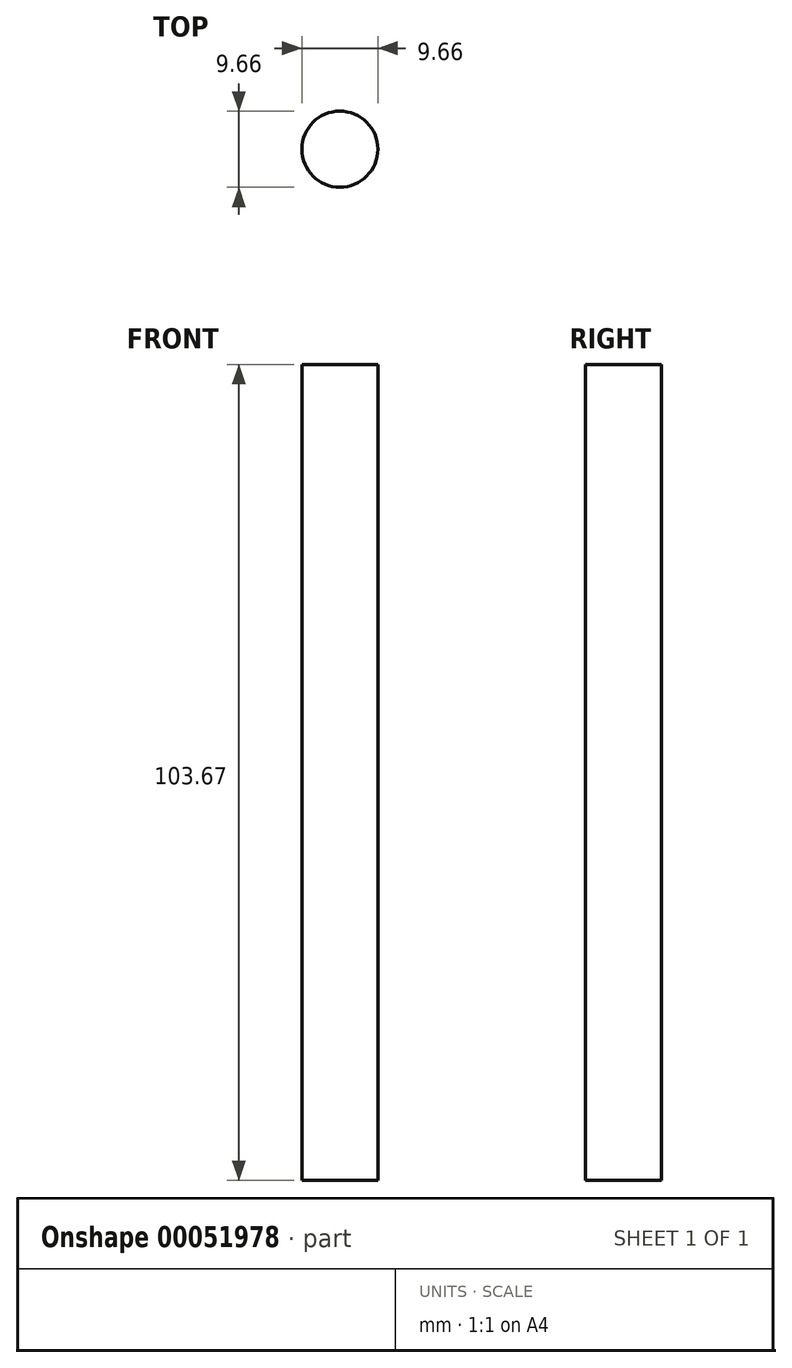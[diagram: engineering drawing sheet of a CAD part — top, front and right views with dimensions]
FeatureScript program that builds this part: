
annotation { "Feature Type Name" : "Feature", "Feature Type Description" : "" }
export const myFeature = defineFeature(function(context is Context, id is Id, definition is map)
    precondition{}
    {
        {
            var Q0;
            Q0=qCreatedBy(makeId("Top.planeOp"),FACE);
            var sketch = newSketch(context, id + "F0", { "sketchPlane" : qUnion([Q0])});
            skCircle(sketch, "E0", {"center": v(-43.8, 34.3) * mm, "radius": 4.83 * mm});
            skSolve(sketch);
        }
        {
            var Q0;
            Q0 = qSketchRegion(id + "F0", true);
            extrude(context, id + "F1", {"entities" : qUnion([Q0]), "depth" : 103.67 * mm});
        }
    });
